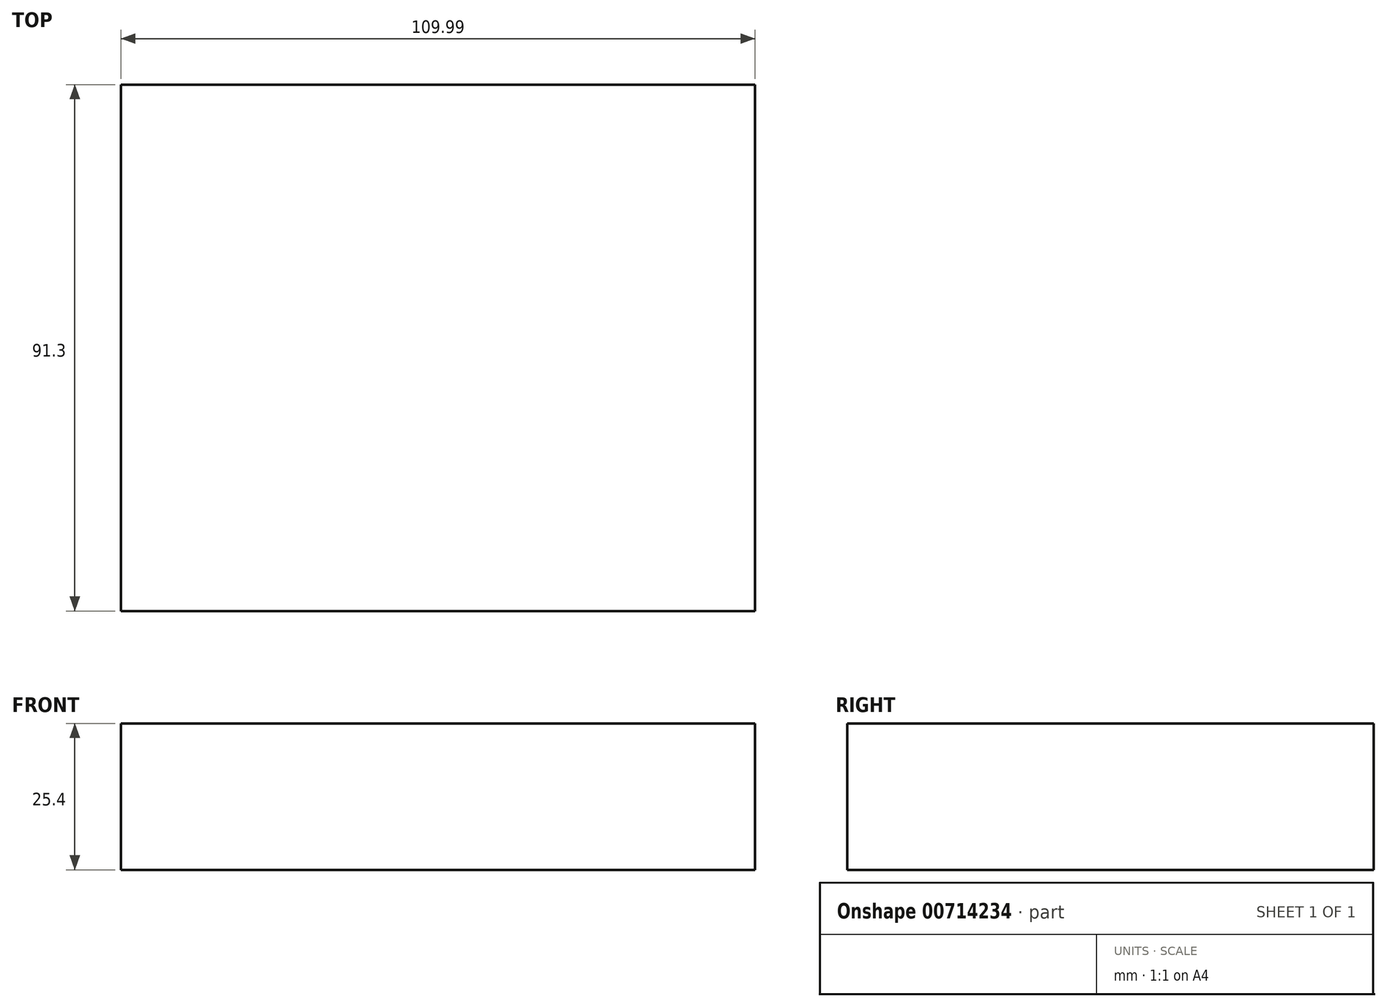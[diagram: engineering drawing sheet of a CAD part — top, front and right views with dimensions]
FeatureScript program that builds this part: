
annotation { "Feature Type Name" : "Feature", "Feature Type Description" : "" }
export const myFeature = defineFeature(function(context is Context, id is Id, definition is map)
    precondition{}
    {
        {
            var Q0;
            Q0=qCreatedBy(makeId("Top.planeOp"),FACE);
            var sketch = newSketch(context, id + "F0", { "sketchPlane" : qUnion([Q0])});
            skLineSegment(sketch, "E0.bottom", {"start": v(50.22, -45.65) * mm, "end": v(-59.77, -45.65) * mm});
            skLineSegment(sketch, "E0.top", {"start": v(50.22, 45.65) * mm, "end": v(-59.77, 45.65) * mm});
            skLineSegment(sketch, "E0.left", {"start": v(50.22, -45.65) * mm, "end": v(50.22, 45.65) * mm});
            skLineSegment(sketch, "E0.right", {"start": v(-59.77, -45.65) * mm, "end": v(-59.77, 45.65) * mm});
            skPoint(sketch, "E0.middle", {"position": v(-4.78, 0) * mm});
            skSolve(sketch);
        }
        {
            var Q0;
            Q0=makeQuery(id+"F0.imprint","IMPRINT",FACE,{"disambiguationData":[TD([[makeQuery(id+"F0.imprint","IMPRINT",EDGE,{"derivedFrom":sQuery(id+"F0.wireOp",EDGE,"E0.bottom")}),-1.0]])]});
            extrude(context, id + "F1", {"entities" : qUnion([Q0]), "depth" : 25.4 * mm, "offsetDistance" : 25.4 * mm});
        }
    });
